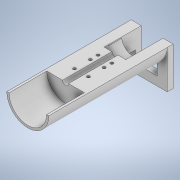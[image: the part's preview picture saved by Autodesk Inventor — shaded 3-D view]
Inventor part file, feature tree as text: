
AUTODESK INVENTOR PART (.ipt)
format: ipt  version: 2022 (Build 260153000, 153)  size: 417,792 bytes
history: native  units: mm
features: extrude x24, sketch x24, fillet x2
ambient origin geometry x8: Origin, YZ Plane, XZ Plane, XY Plane, X Axis, Y Axis, Z Axis, Center Point
bodies: Solid1 (feature_tree)
feature tree (50):
  extrude  "Extrusion1"  Depth=70.0mm
  extrude  "Extrusion2"  Depth=6.0mm TaperAngle=0.0deg
  extrude  "Extrusion3"  Depth=3.0mm
  fillet  "Fillet1"  Radius=40.0mm
  extrude  "Extrusion4"  Depth=4.0mm
  extrude  "Extrusion5"  Depth=5.0mm TaperAngle=0.0deg
  extrude  "Extrusion6"  Depth=11.0mm
  extrude  "Extrusion7"  Depth=11.0mm
  extrude  "Extrusion8"  Depth=24.0mm TaperAngle=0.0deg
  extrude  "Extrusion9"  Depth=6.0mm TaperAngle=0.0deg
  extrude  "Extrusion10"  Depth=13.8mm
  extrude  "Extrusion11"  Depth=13.8mm TaperAngle=0.0deg
  extrude  "Extrusion12"  Depth=50.0mm TaperAngle=0.0deg
  fillet  "Fillet3"  Radius=50.0mm
  extrude  "Extrusion19"  Depth=38.0mm
  extrude  "Extrusion20"  Depth=6.2mm TaperAngle=0.0deg
  extrude  "Extrusion21"  Depth=10.0mm TaperAngle=0.0deg
  extrude  "Extrusion22"  Depth=10.0mm TaperAngle=0.0deg
  extrude  "Extrusion23"  Depth=10.0mm TaperAngle=0.0deg
  extrude  "Extrusion24"  Depth=150.0mm TaperAngle=0.0deg
  extrude  "Extrusion25"  Depth=10.0mm TaperAngle=0.0deg
  extrude  "Extrusion27"  Depth=9.0mm TaperAngle=0.0deg
  extrude  "Extrusion28"  [1 undecoded]
  extrude  "Extrusion29"  [1 undecoded]
  extrude  "Extrusion30"  [1 undecoded]
  extrude  "Extrusion31"  [1 undecoded]
  sketch  "Sketch1"  dims[d0=62.0mm d1=70.0mm]
  sketch  "Sketch2"  dims[d2=6.0mm d3=40.0mm d4=0.0mm]
  sketch  "Sketch3"  dims[d5=62.0mm d9=3.0mm d10=40.0mm d12=360.0deg]
  sketch  "Sketch4"  dims[d14=40.0mm d15=0.0mm d16=4.0mm]
  sketch  "Sketch5"  dims[d18=11.5mm d19=5.0mm d20=0.0mm]
  sketch  "Sketch6"  dims[d21=8.0mm d22=11.0mm]
  sketch  "Sketch8"  dims[d23=11.0mm d24=5.0mm]
  sketch  "Sketch9"  dims[d25=5.0mm d26=24.0mm d27=0.0mm]
  sketch  "Sketch10"  dims[d29=6.0mm d30=6.0mm d31=0.0mm]
  sketch  "Sketch11"  dims[d32=13.8mm d33=0.0mm d37=33.7mm]
  sketch  "Sketch12"  dims[d38=11.0mm d39=13.8mm d40=0.0mm]
  sketch  "Sketch13"  dims[d41=6.0mm d42=50.0mm d43=0.0mm d44=50.0mm d45=0.0mm]
  sketch  "Sketch20"  dims[d47=36.0mm d48=0.0mm d49=38.0mm]
  sketch  "Sketch21"  dims[d50=32.0mm d51=0.0mm d52=6.2mm d53=0.0mm]
  sketch  "Sketch22"  dims[d63=1.0mm d69=10.0mm d70=0.0mm]
  sketch  "Sketch23"  dims[d71=10.0mm d72=0.0mm d73=10.0mm d74=0.0mm]
  sketch  "Sketch24"  dims[d75=10.0mm d76=0.0mm d77=10.0mm d78=0.0mm]
  sketch  "Sketch25"  dims[d79=150.0mm d80=0.0mm d81=150.0mm d82=0.0mm]
  sketch  "Sketch26"  dims[d90=0.0mm d91=0.0mm d92=10.0mm d93=0.0mm]
  sketch  "Sketch28"  dims[d94=18.6mm d95=0.0mm d96=9.0mm d97=0.0mm]
  sketch  "Sketch29"  dims[d98=4.0mm d99=0.0mm]
  sketch  "Sketch30"
  sketch  "Sketch31"
  sketch  "Sketch32"
note: 4 required parameter values undecoded (feature->parameter linkage not recoverable at this tier; creation-order binding heuristic only, values carry confidence <= 0.55)
